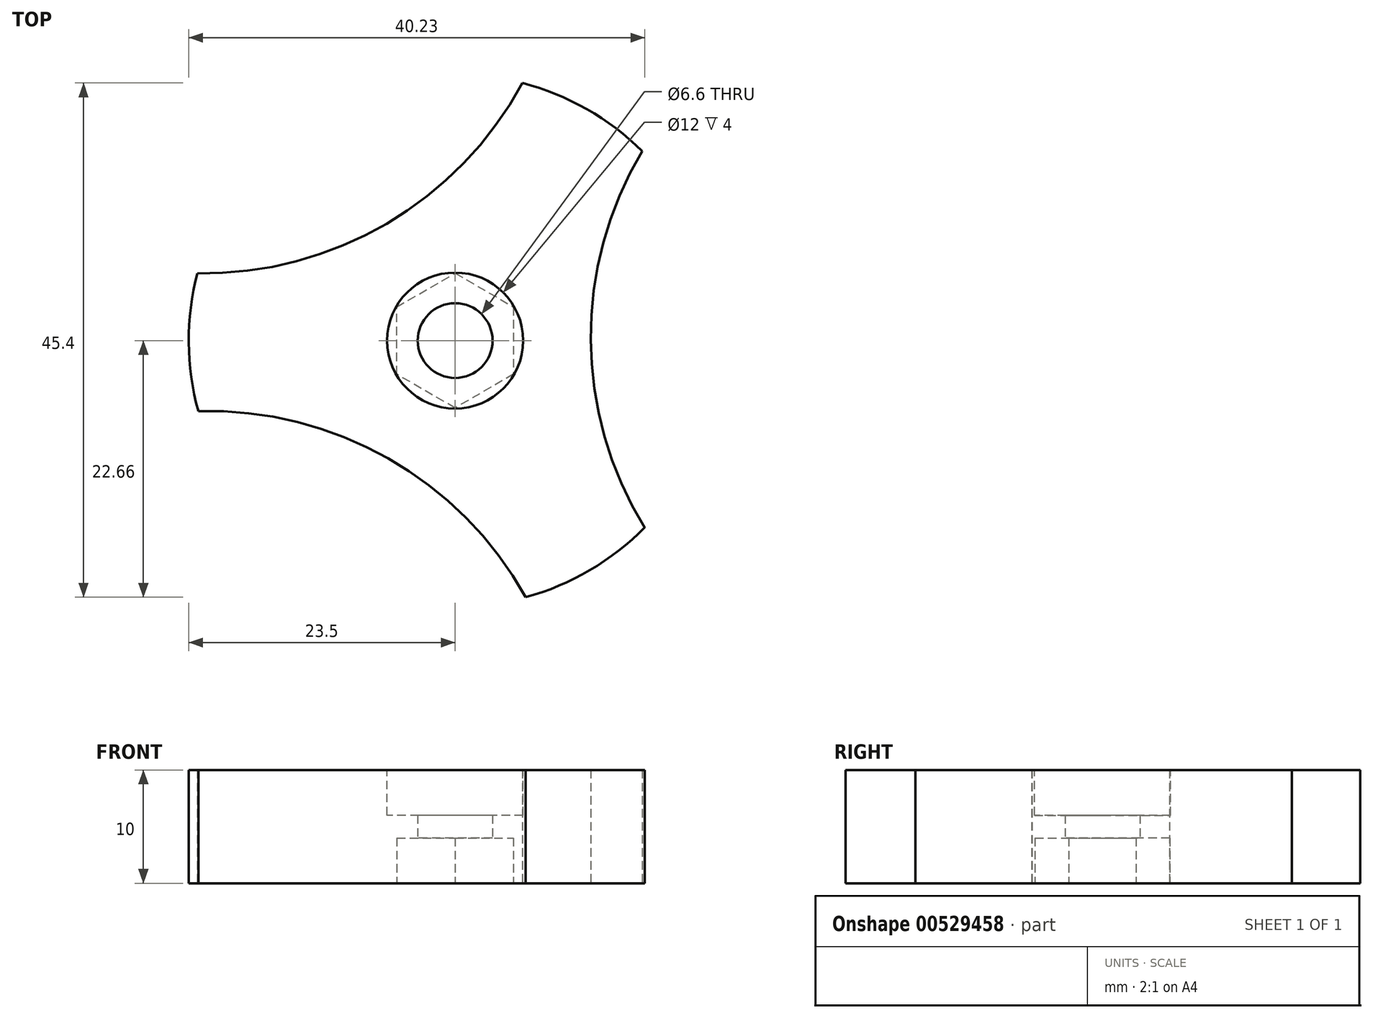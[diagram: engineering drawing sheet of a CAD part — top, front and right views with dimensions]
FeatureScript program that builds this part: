
annotation { "Feature Type Name" : "Feature", "Feature Type Description" : "" }
export const myFeature = defineFeature(function(context is Context, id is Id, definition is map)
    precondition{}
    {
        {
            var Q0;
            Q0=qCreatedBy(makeId("Top.planeOp"),FACE);
            var sketch = newSketch(context, id + "F0", { "sketchPlane" : qUnion([Q0])});
            skCircle(sketch, "E0", {"center": v(0, 0) * mm, "radius": 23.5 * mm});
            skCircle(sketch, "E1.cCircle", {"center": v(0, 0) * mm, "radius": 22.7 * mm, "construction": true});
            skLineSegment(sketch, "E1.0", {"start": v(5.93, 22.74) * mm, "end": v(16.5, 16.73) * mm});
            skLineSegment(sketch, "E1.1", {"start": v(16.5, 16.73) * mm, "end": v(22.66, 6.23) * mm});
            skLineSegment(sketch, "E1.2", {"start": v(22.66, 6.23) * mm, "end": v(22.74, -5.93) * mm});
            skLineSegment(sketch, "E1.3", {"start": v(22.74, -5.93) * mm, "end": v(16.73, -16.5) * mm});
            skLineSegment(sketch, "E1.4", {"start": v(16.73, -16.5) * mm, "end": v(6.23, -22.66) * mm});
            skLineSegment(sketch, "E1.5", {"start": v(6.23, -22.66) * mm, "end": v(-5.93, -22.74) * mm});
            skLineSegment(sketch, "E1.6", {"start": v(-5.93, -22.74) * mm, "end": v(-16.5, -16.73) * mm});
            skLineSegment(sketch, "E1.7", {"start": v(-16.5, -16.73) * mm, "end": v(-22.66, -6.23) * mm});
            skLineSegment(sketch, "E1.8", {"start": v(-22.66, -6.23) * mm, "end": v(-22.74, 5.93) * mm});
            skLineSegment(sketch, "E1.9", {"start": v(-22.74, 5.93) * mm, "end": v(-16.73, 16.5) * mm});
            skLineSegment(sketch, "E1.10", {"start": v(-16.73, 16.5) * mm, "end": v(-6.23, 22.66) * mm});
            skLineSegment(sketch, "E1.11", {"start": v(-6.23, 22.66) * mm, "end": v(5.93, 22.74) * mm});
            skPoint(sketch, "E1.0.midPoint", {"position": v(11.22, 19.73) * mm});
            skArc(sketch, "E2", {"start": v(-22.74, 5.93) * mm, "mid": v(-6.05, 10.32) * mm, "end": v(5.93, 22.74) * mm});
            skArc(sketch, "E3", {"start": v(16.5, 16.73) * mm, "mid": v(11.96, 0.08) * mm, "end": v(16.73, -16.5) * mm});
            skArc(sketch, "E4", {"start": v(6.23, -22.66) * mm, "mid": v(-5.91, -10.4) * mm, "end": v(-22.66, -6.23) * mm});
            skCircle(sketch, "E5.cCircle", {"center": v(0, 0) * mm, "radius": 5.15 * mm, "construction": true});
            skLineSegment(sketch, "E5.0", {"start": v(0, 5.95) * mm, "end": v(5.15, 2.97) * mm});
            skLineSegment(sketch, "E5.1", {"start": v(5.15, 2.97) * mm, "end": v(5.15, -2.97) * mm});
            skLineSegment(sketch, "E5.2", {"start": v(5.15, -2.97) * mm, "end": v(0, -5.95) * mm});
            skLineSegment(sketch, "E5.3", {"start": v(0, -5.95) * mm, "end": v(-5.15, -2.97) * mm});
            skLineSegment(sketch, "E5.4", {"start": v(-5.15, -2.97) * mm, "end": v(-5.15, 2.97) * mm});
            skLineSegment(sketch, "E5.5", {"start": v(-5.15, 2.97) * mm, "end": v(0, 5.95) * mm});
            skPoint(sketch, "E5.0.midPoint", {"position": v(2.57, 4.46) * mm});
            skLineSegment(sketch, "E6", {"start": v(0, 0) * mm, "end": v(0, 4.15) * mm, "construction": true});
            skSolve(sketch);
        }
        {
            var Q0;
            {var subQ0=sQuery(id+"F0.wireOp",EDGE,"E1.0");Q0=makeQuery(id+"F0.imprint","IMPRINT",FACE,{"disambiguationData":[TD([[makeQuery(id+"F0.imprint","IMPRINT",EDGE,{"derivedFrom":subQ0}),1.0]])]});}
            var Q1;
            {var subQ0=sQuery(id+"F0.wireOp",EDGE,"E1.8");Q1=makeQuery(id+"F0.imprint","IMPRINT",FACE,{"disambiguationData":[TD([[makeQuery(id+"F0.imprint","IMPRINT",EDGE,{"derivedFrom":subQ0}),1.0]])]});}
            var Q2;
            {var subQ0=sQuery(id+"F0.wireOp",EDGE,"E1.4");Q2=makeQuery(id+"F0.imprint","IMPRINT",FACE,{"disambiguationData":[TD([[makeQuery(id+"F0.imprint","IMPRINT",EDGE,{"derivedFrom":subQ0}),1.0]])]});}
            var Q3;
            Q3=makeQuery(id+"F0.imprint","IMPRINT",FACE,{"disambiguationData":[TD([[makeQuery(id+"F0.imprint","IMPRINT",EDGE,{"derivedFrom":sQuery(id+"F0.wireOp",EDGE,"E1.0")}),-1.0]])]});
            var Q4;
            Q4=makeQuery(id+"F0.imprint","IMPRINT",FACE,{"disambiguationData":[TD([[makeQuery(id+"F0.imprint","IMPRINT",EDGE,{"derivedFrom":sQuery(id+"F0.wireOp",EDGE,"E5.0")}),-1.0]])]});
            extrude(context, id + "F1", {"entities" : qUnion([Q0, Q1, Q2, Q3, Q4]), "depth" : 10 * mm, "offsetDistance" : 25 * mm});
        }
        {
            var Q0;
            Q0=makeQuery(id+"F0.imprint","IMPRINT",FACE,{"disambiguationData":[TD([[makeQuery(id+"F0.imprint","IMPRINT",EDGE,{"derivedFrom":sQuery(id+"F0.wireOp",EDGE,"E5.0")}),-1.0]])]});
            extrude(context, id + "F2", {"entities" : qUnion([Q0]), "operationType" : NewBodyOperationType.REMOVE, "depth" : 4 * mm, "offsetDistance" : 25 * mm});
        }
        {
            var Q0;
            Q0=sQuery(id+"F0.wireOp",VERTEX,"E6.start");
            var Q1;
            Q1=makeQuery(id+"F1.opExtrude","SWEPT_BODY",BODY,{"disambiguationData":[OSD([sQuery(id+"F0.wireOp",EDGE,"E0"),sQuery(id+"F0.wireOp",EDGE,"E2"),sQuery(id+"F0.wireOp",EDGE,"E3"),sQuery(id+"F0.wireOp",EDGE,"E4")])]});
            hole(context, id + "F3", {"style" : HoleStyle.SIMPLE, "endStyle" : HoleEndStyle.THROUGH, "oppositeDirection" : true, "holeDiameter" : 6.6 * mm, "majorDiameter" : 5 * mm, "isTappedThrough" : true, "tappedDepth" : 10.5 * mm, "tapClearance" : 3, "locations" : qUnion([Q0]), "scope" : qUnion([Q1])});
        }
        {
            var Q0;
            Q0=makeQuery(id+"F1.opExtrude","CAP_FACE",FACE,{"disambiguationData":[OSD([sQuery(id+"F0.wireOp",EDGE,"E0"),sQuery(id+"F0.wireOp",EDGE,"E2"),sQuery(id+"F0.wireOp",EDGE,"E3"),sQuery(id+"F0.wireOp",EDGE,"E4")])],"isStart":false});
            var sketch = newSketch(context, id + "F4", { "sketchPlane" : qUnion([Q0])});
            skPoint(sketch, "E7", {"position": v(0, 0) * mm});
            skCircle(sketch, "E8", {"center": v(0, 0) * mm, "radius": 6 * mm});
            skSolve(sketch);
        }
        {
            var Q0;
            Q0=makeQuery(id+"F4.imprint","IMPRINT",FACE,{"disambiguationData":[TD([[makeQuery(id+"F4.imprint","IMPRINT",EDGE,{"derivedFrom":sQuery(id+"F4.wireOp",EDGE,"E8")}),1.0]])]});
            extrude(context, id + "F5", {"entities" : qUnion([Q0]), "operationType" : NewBodyOperationType.REMOVE, "oppositeDirection" : true, "depth" : 4 * mm, "offsetDistance" : 25 * mm});
        }
    });
